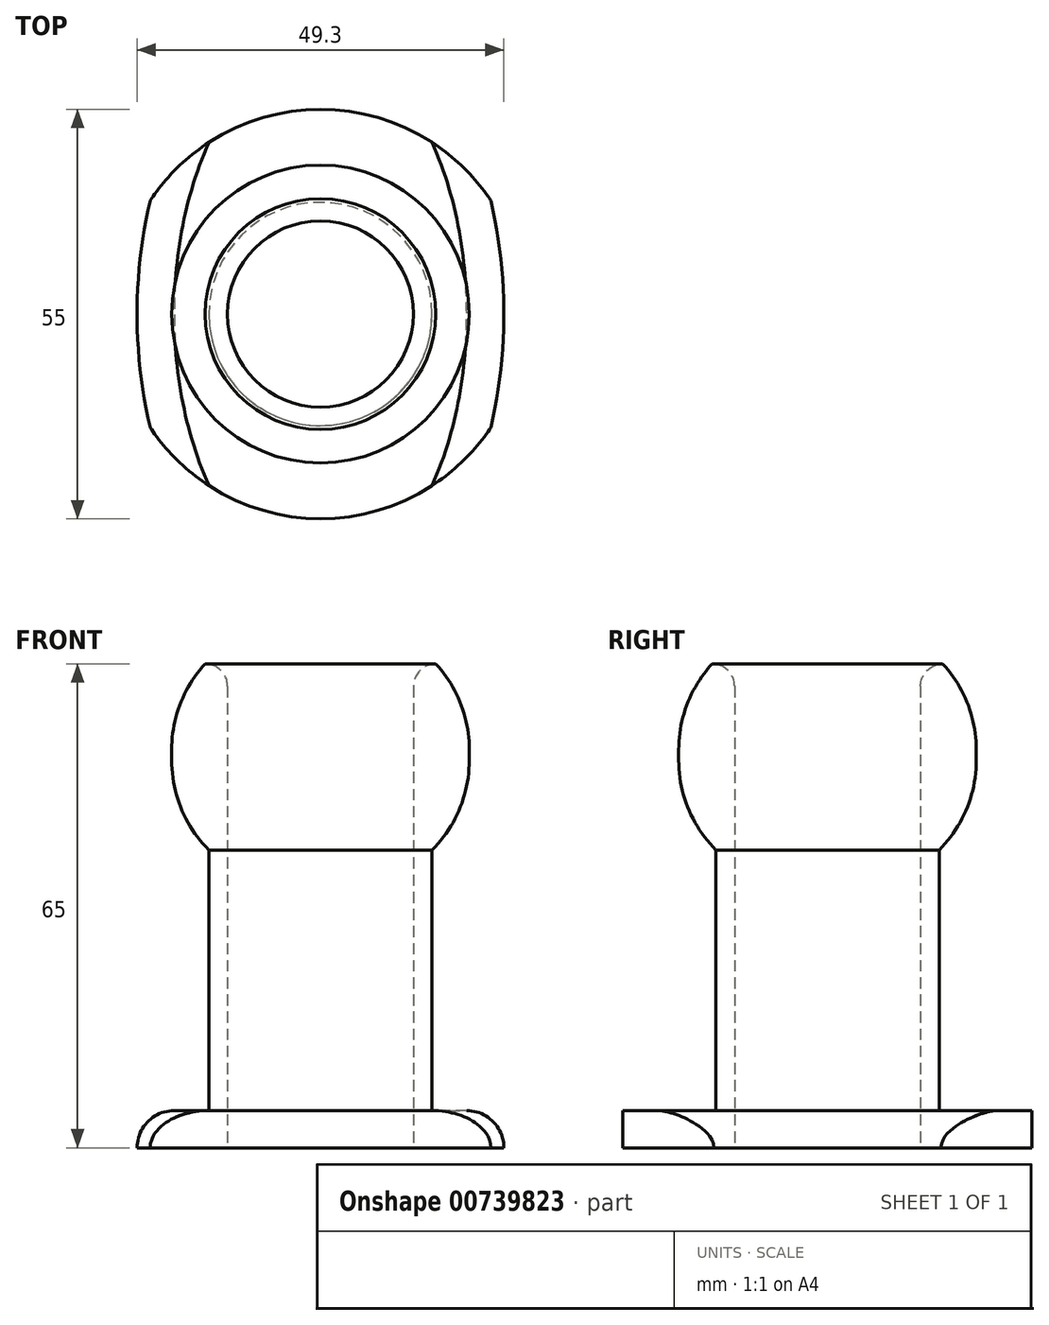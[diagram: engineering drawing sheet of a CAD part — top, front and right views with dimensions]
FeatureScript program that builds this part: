
annotation { "Feature Type Name" : "Feature", "Feature Type Description" : "" }
export const myFeature = defineFeature(function(context is Context, id is Id, definition is map)
    precondition{}
    {
        {
            var Q0;
            Q0=qCreatedBy(makeId("Top.planeOp"),FACE);
            var sketch = newSketch(context, id + "F0", { "sketchPlane" : qUnion([Q0])});
            skCircle(sketch, "E0", {"center": v(0, 0) * mm, "radius": 20 * mm});
            skEllipse(sketch, "E1", {"center": v(0, 0) * mm, "majorRadius": 41.12 * mm, "minorRadius": 24.65 * mm, "majorAxis": v(0, -1)});
            skCircle(sketch, "E2", {"center": v(0, 0) * mm, "radius": 15 * mm});
            skCircle(sketch, "E3", {"center": v(0, 0) * mm, "radius": 12.5 * mm});
            skCircle(sketch, "E4", {"center": v(0, 0) * mm, "radius": 27.5 * mm});
            skSolve(sketch);
        }
        {
            var Q0;
            {var subQ0=sQuery(id+"F0.wireOp",EDGE,"E4");var subQ1=sQuery(id+"F0.wireOp",EDGE,"E1");var subQ2=makeQuery(id+"F0.imprint","INTERSECT",VERTEX,{"disambiguationData":[OD(0.0)],"derivedFrom":[subQ1,subQ0]});Q0=makeQuery(id+"F0.imprint","IMPRINT",FACE,{"disambiguationData":[TD([[makeQuery(id+"F0.imprint","IMPRINT",EDGE,{"disambiguationData":[TD([[subQ2,-1.0]])],"derivedFrom":subQ1}),1.0]])]});}
            var Q1;
            {var subQ0=sQuery(id+"F0.wireOp",EDGE,"E4");var subQ1=sQuery(id+"F0.wireOp",EDGE,"E1");var subQ2=makeQuery(id+"F0.imprint","INTERSECT",VERTEX,{"disambiguationData":[OD(1.0)],"derivedFrom":[subQ1,subQ0]});Q1=makeQuery(id+"F0.imprint","IMPRINT",FACE,{"disambiguationData":[TD([[makeQuery(id+"F0.imprint","IMPRINT",EDGE,{"disambiguationData":[TD([[subQ2,1.0]])],"derivedFrom":subQ1}),1.0]])]});}
            var Q2;
            Q2=makeQuery(id+"F0.imprint","IMPRINT",FACE,{"disambiguationData":[TD([[makeQuery(id+"F0.imprint","IMPRINT",EDGE,{"derivedFrom":sQuery(id+"F0.wireOp",EDGE,"E0")}),-1.0]])]});
            var Q3;
            Q3=makeQuery(id+"F0.imprint","IMPRINT",FACE,{"disambiguationData":[TD([[makeQuery(id+"F0.imprint","IMPRINT",EDGE,{"derivedFrom":sQuery(id+"F0.wireOp",EDGE,"E0")}),1.0]])]});
            extrude(context, id + "F1", {"entities" : qUnion([Q0, Q1, Q2, Q3]), "depth" : 5 * mm, "offsetDistance" : 25 * mm});
        }
        {
            var Q0;
            Q0=makeQuery(id+"F1.opExtrude","CAP_EDGE",EDGE,{"disambiguationData":[OSD([sQuery(id+"F0.wireOp",EDGE,"E1")])],"isStart":false});
            fillet(context, id + "F2", {"entities" : qUnion([Q0]), "radius" : 5 * mm, "tangentPropagation" : true, "allowEdgeOverflow" : false});
        }
        {
            var Q0;
            Q0=makeQuery(id+"F0.imprint","IMPRINT",FACE,{"disambiguationData":[TD([[makeQuery(id+"F0.imprint","IMPRINT",EDGE,{"derivedFrom":sQuery(id+"F0.wireOp",EDGE,"E0")}),1.0]])]});
            extrude(context, id + "F3", {"entities" : qUnion([Q0]), "depth" : 65 * mm, "offsetDistance" : 25 * mm, "hasSecondDirection" : true, "secondDirectionOppositeDirection" : false, "secondDirectionDepth" : 40 * mm});
        }
        {
            var Q0;
            Q0=makeQuery(id+"F0.imprint","IMPRINT",FACE,{"disambiguationData":[TD([[makeQuery(id+"F0.imprint","IMPRINT",EDGE,{"derivedFrom":sQuery(id+"F0.wireOp",EDGE,"E2")}),1.0]])]});
            extrude(context, id + "F4", {"entities" : qUnion([Q0]), "operationType" : NewBodyOperationType.ADD, "depth" : 65 * mm, "offsetDistance" : 25 * mm});
        }
        {
            var Q0;
            Q0=makeQuery(id+"F4.opExtrude","CAP_EDGE",EDGE,{"disambiguationData":[OSD([sQuery(id+"F0.wireOp",EDGE,"E3")])],"isStart":false});
            fillet(context, id + "F5", {"entities" : qUnion([Q0]), "radius" : 3 * mm, "tangentPropagation" : true, "allowEdgeOverflow" : false});
        }
        {
            var Q0;
            Q0=makeQuery(id+"F3.opExtrude","SWEPT_FACE",FACE,{"disambiguationData":[OSD([sQuery(id+"F0.wireOp",EDGE,"E0")])]});
            fillet(context, id + "F6", {"entities" : qUnion([Q0]), "radius" : 17 * mm, "tangentPropagation" : true, "allowEdgeOverflow" : false});
        }
    });
